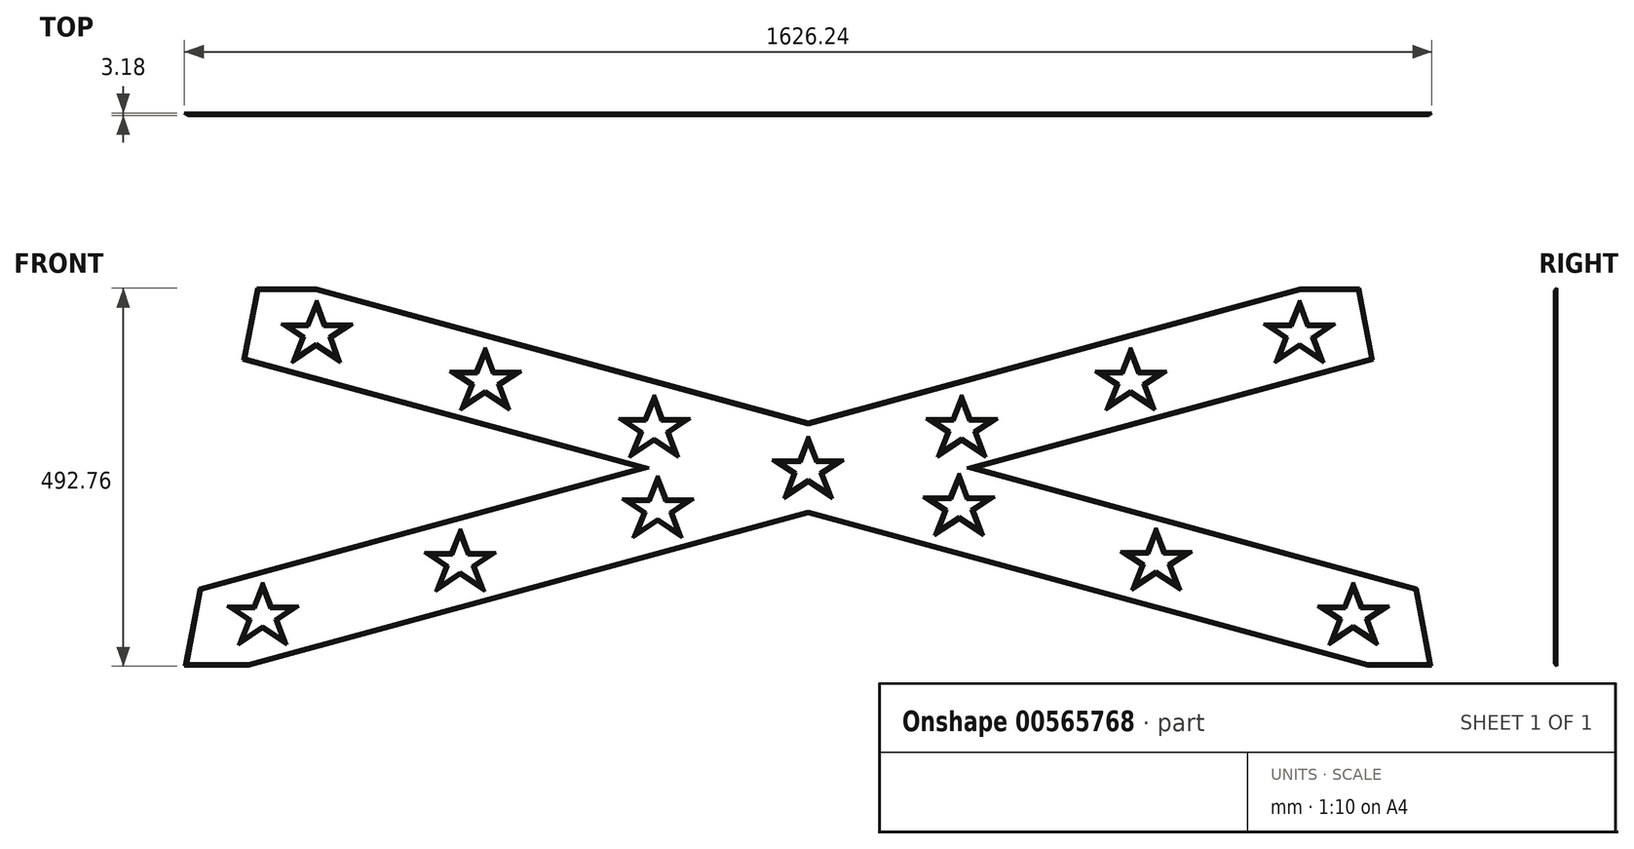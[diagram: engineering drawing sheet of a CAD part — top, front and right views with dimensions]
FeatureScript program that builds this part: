
annotation { "Feature Type Name" : "Feature", "Feature Type Description" : "" }
export const myFeature = defineFeature(function(context is Context, id is Id, definition is map)
    precondition{}
    {
        {
            var Q0;
            Q0=qCreatedBy(makeId("Front.planeOp"),FACE);
            var sketch = newSketch(context, id + "F0", { "sketchPlane" : qUnion([Q0])});
            skLineSegment(sketch, "E0", {"start": v(-830, -263.65) * mm, "end": v(830, -263.65) * mm});
            skLineSegment(sketch, "E1", {"start": v(830, -263.65) * mm, "end": v(730.63, 257.05) * mm});
            skLineSegment(sketch, "E2", {"start": v(730.63, 257.05) * mm, "end": v(-730.63, 257.05) * mm});
            skLineSegment(sketch, "E3", {"start": v(-730.63, 257.05) * mm, "end": v(-830, -263.65) * mm});
            skLineSegment(sketch, "E4", {"start": v(-738.12, 143.28) * mm, "end": v(-792.33, -140.76) * mm});
            skLineSegment(sketch, "E5", {"start": v(-705.17, -249.68) * mm, "end": v(705.17, -249.68) * mm});
            skLineSegment(sketch, "E6", {"start": v(-617.48, 243.08) * mm, "end": v(617.48, 243.08) * mm});
            skLineSegment(sketch, "E7", {"start": v(792.33, -140.76) * mm, "end": v(738.12, 143.28) * mm});
            skLineSegment(sketch, "E8", {"start": v(-738.12, 143.28) * mm, "end": v(-243.6, 8.64) * mm});
            skLineSegment(sketch, "E9", {"start": v(792.33, -140.76) * mm, "end": v(243.6, 8.64) * mm});
            skLineSegment(sketch, "E10", {"start": v(-792.33, -140.76) * mm, "end": v(-243.6, 8.64) * mm});
            skLineSegment(sketch, "E11", {"start": v(738.12, 143.28) * mm, "end": v(243.6, 8.64) * mm});
            skLineSegment(sketch, "E12.trimOffspring", {"start": v(0, 74.96) * mm, "end": v(617.48, 243.08) * mm});
            skLineSegment(sketch, "E13.trimOffspring", {"start": v(0, -57.68) * mm, "end": v(705.17, -249.68) * mm});
            skLineSegment(sketch, "E14.trimOffspring", {"start": v(0, 74.96) * mm, "end": v(-617.48, 243.08) * mm});
            skLineSegment(sketch, "E15.trimOffspring", {"start": v(0, -57.68) * mm, "end": v(-705.17, -249.68) * mm});
            skPoint(sketch, "E16.orphan", {"position": v(813.12, -249.68) * mm});
            skPoint(sketch, "E17.orphan", {"position": v(719.08, 243.08) * mm});
            skPoint(sketch, "E18.orphan", {"position": v(-719.08, 243.08) * mm});
            skPoint(sketch, "E19.orphan", {"position": v(-813.12, -249.68) * mm});
            skSolve(sketch);
        }
        {
            var Q0;
            Q0=makeQuery(id+"F0.imprint","IMPRINT",FACE,{"disambiguationData":[TD([[makeQuery(id+"F0.imprint","IMPRINT",EDGE,{"derivedFrom":sQuery(id+"F0.wireOp",EDGE,"E0")}),1.0]])]});
            var sketch = newSketch(context, id + "F1", { "sketchPlane" : qUnion([Q0])});
            skLineSegment(sketch, "E20", {"start": v(-736.93, 149.54) * mm, "end": v(-719.08, 243.08) * mm});
            skLineSegment(sketch, "E21", {"start": v(-719.08, 243.08) * mm, "end": v(-641.65, 243.08) * mm});
            skLineSegment(sketch, "E22", {"start": v(-641.65, 243.08) * mm, "end": v(0, 68.38) * mm});
            skLineSegment(sketch, "E23", {"start": v(0, 68.38) * mm, "end": v(641.65, 243.08) * mm});
            skLineSegment(sketch, "E24", {"start": v(641.65, 243.08) * mm, "end": v(719.08, 243.08) * mm});
            skLineSegment(sketch, "E25", {"start": v(719.08, 243.08) * mm, "end": v(736.93, 149.54) * mm});
            skLineSegment(sketch, "E26", {"start": v(736.93, 149.54) * mm, "end": v(219.43, 8.64) * mm});
            skLineSegment(sketch, "E27", {"start": v(219.43, 8.64) * mm, "end": v(793.66, -147.7) * mm});
            skLineSegment(sketch, "E28", {"start": v(793.66, -147.7) * mm, "end": v(813.12, -249.68) * mm});
            skLineSegment(sketch, "E29", {"start": v(813.12, -249.68) * mm, "end": v(729.34, -249.68) * mm});
            skLineSegment(sketch, "E30", {"start": v(729.34, -249.68) * mm, "end": v(0, -51.1) * mm});
            skLineSegment(sketch, "E31", {"start": v(0, -51.1) * mm, "end": v(-729.34, -249.68) * mm});
            skLineSegment(sketch, "E32", {"start": v(-729.34, -249.68) * mm, "end": v(-813.12, -249.68) * mm});
            skLineSegment(sketch, "E33", {"start": v(-813.12, -249.68) * mm, "end": v(-793.66, -147.7) * mm});
            skLineSegment(sketch, "E34", {"start": v(-793.66, -147.7) * mm, "end": v(-219.43, 8.64) * mm});
            skLineSegment(sketch, "E35", {"start": v(-219.43, 8.64) * mm, "end": v(-736.93, 149.54) * mm});
            skSolve(sketch);
        }
        {
            var Q0;
            Q0 = qSketchRegion(id + "F1", true);
            extrude(context, id + "F2", {"entities" : qUnion([Q0]), "depth" : 3.17 * mm, "offsetDistance" : 25.4 * mm});
        }
        {
            var Q0;
            Q0=makeQuery(id+"F2.opExtrude","CAP_FACE",FACE,{"disambiguationData":[OSD([sQuery(id+"F1.wireOp",EDGE,"E20"),sQuery(id+"F1.wireOp",EDGE,"E21"),sQuery(id+"F1.wireOp",EDGE,"E22"),sQuery(id+"F1.wireOp",EDGE,"E23"),sQuery(id+"F1.wireOp",EDGE,"E24"),sQuery(id+"F1.wireOp",EDGE,"E25"),sQuery(id+"F1.wireOp",EDGE,"E26"),sQuery(id+"F1.wireOp",EDGE,"E27"),sQuery(id+"F1.wireOp",EDGE,"E28"),sQuery(id+"F1.wireOp",EDGE,"E29"),sQuery(id+"F1.wireOp",EDGE,"E30"),sQuery(id+"F1.wireOp",EDGE,"E31"),sQuery(id+"F1.wireOp",EDGE,"E32"),sQuery(id+"F1.wireOp",EDGE,"E33"),sQuery(id+"F1.wireOp",EDGE,"E34"),sQuery(id+"F1.wireOp",EDGE,"E35")])],"isStart":false});
            var sketch = newSketch(context, id + "F3", { "sketchPlane" : qUnion([Q0])});
            skLineSegment(sketch, "E36.3.0.0", {"start": v(-651.4, 193.24) * mm, "end": v(-641.14, 218.64) * mm});
            skLineSegment(sketch, "E36.3.0.1", {"start": v(-631.77, 193.24) * mm, "end": v(-604.51, 193.24) * mm});
            skLineSegment(sketch, "E36.3.0.2", {"start": v(-641.14, 218.64) * mm, "end": v(-631.77, 193.24) * mm});
            skLineSegment(sketch, "E36.3.0.3", {"start": v(-604.51, 193.24) * mm, "end": v(-625.1, 179.5) * mm});
            skLineSegment(sketch, "E36.3.0.4", {"start": v(-625.1, 179.5) * mm, "end": v(-615.74, 154.1) * mm});
            skLineSegment(sketch, "E36.3.0.5", {"start": v(-615.74, 154.1) * mm, "end": v(-641.14, 171.05) * mm});
            skLineSegment(sketch, "E36.3.0.6", {"start": v(-641.14, 171.05) * mm, "end": v(-666.54, 154.1) * mm});
            skLineSegment(sketch, "E36.3.0.7", {"start": v(-666.54, 154.1) * mm, "end": v(-656.28, 179.5) * mm});
            skLineSegment(sketch, "E36.3.0.8", {"start": v(-656.28, 179.5) * mm, "end": v(-676.87, 193.24) * mm});
            skLineSegment(sketch, "E36.3.0.9", {"start": v(-676.87, 193.24) * mm, "end": v(-651.4, 193.24) * mm});
            skLineSegment(sketch, "E37.1.0.0", {"start": v(-446.42, 92.4) * mm, "end": v(-436.16, 117.8) * mm});
            skLineSegment(sketch, "E37.1.0.1", {"start": v(-421.02, 109.36) * mm, "end": v(-446.42, 92.4) * mm});
            skLineSegment(sketch, "E37.1.0.2", {"start": v(-395.62, 92.4) * mm, "end": v(-421.02, 109.36) * mm});
            skLineSegment(sketch, "E37.1.0.3", {"start": v(-404.99, 117.8) * mm, "end": v(-395.62, 92.4) * mm});
            skLineSegment(sketch, "E37.1.0.4", {"start": v(-384.4, 131.55) * mm, "end": v(-404.99, 117.8) * mm});
            skLineSegment(sketch, "E37.1.0.5", {"start": v(-411.65, 131.55) * mm, "end": v(-384.4, 131.55) * mm});
            skLineSegment(sketch, "E37.1.0.6", {"start": v(-421.02, 156.95) * mm, "end": v(-411.65, 131.55) * mm});
            skLineSegment(sketch, "E37.1.0.7", {"start": v(-431.28, 131.55) * mm, "end": v(-421.02, 156.95) * mm});
            skLineSegment(sketch, "E37.1.0.8", {"start": v(-456.75, 131.55) * mm, "end": v(-431.28, 131.55) * mm});
            skLineSegment(sketch, "E37.1.0.9", {"start": v(-436.16, 117.8) * mm, "end": v(-456.75, 131.55) * mm});
            skLineSegment(sketch, "E37.2.0.0", {"start": v(-226.3, 30.71) * mm, "end": v(-216.04, 56.11) * mm});
            skLineSegment(sketch, "E37.2.0.1", {"start": v(-200.9, 47.67) * mm, "end": v(-226.3, 30.71) * mm});
            skLineSegment(sketch, "E37.2.0.2", {"start": v(-175.5, 30.71) * mm, "end": v(-200.9, 47.67) * mm});
            skLineSegment(sketch, "E37.2.0.3", {"start": v(-184.87, 56.11) * mm, "end": v(-175.5, 30.71) * mm});
            skLineSegment(sketch, "E37.2.0.4", {"start": v(-164.27, 69.86) * mm, "end": v(-184.87, 56.11) * mm});
            skLineSegment(sketch, "E37.2.0.5", {"start": v(-191.53, 69.86) * mm, "end": v(-164.27, 69.86) * mm});
            skLineSegment(sketch, "E37.2.0.6", {"start": v(-200.9, 95.26) * mm, "end": v(-191.53, 69.86) * mm});
            skLineSegment(sketch, "E37.2.0.7", {"start": v(-211.16, 69.86) * mm, "end": v(-200.9, 95.26) * mm});
            skLineSegment(sketch, "E37.2.0.8", {"start": v(-236.63, 69.86) * mm, "end": v(-211.16, 69.86) * mm});
            skLineSegment(sketch, "E37.2.0.9", {"start": v(-216.04, 56.11) * mm, "end": v(-236.63, 69.86) * mm});
            skLineSegment(sketch, "E37.direction1", {"start": v(-666.54, 154.1) * mm, "end": v(-446.42, 92.4) * mm, "construction": true});
            skLineSegment(sketch, "E38.3.0.0", {"start": v(-721.15, -174.63) * mm, "end": v(-711.11, -149.23) * mm});
            skLineSegment(sketch, "E38.3.0.1", {"start": v(-701.51, -174.63) * mm, "end": v(-674.72, -174.63) * mm});
            skLineSegment(sketch, "E38.3.0.2", {"start": v(-711.11, -149.23) * mm, "end": v(-701.51, -174.63) * mm});
            skLineSegment(sketch, "E38.3.0.3", {"start": v(-674.72, -174.63) * mm, "end": v(-695.31, -188.38) * mm});
            skLineSegment(sketch, "E38.3.0.4", {"start": v(-695.31, -188.38) * mm, "end": v(-685.71, -213.78) * mm});
            skLineSegment(sketch, "E38.3.0.5", {"start": v(-685.71, -213.78) * mm, "end": v(-711.11, -196.82) * mm});
            skLineSegment(sketch, "E38.3.0.6", {"start": v(-711.11, -196.82) * mm, "end": v(-736.51, -213.78) * mm});
            skLineSegment(sketch, "E38.3.0.7", {"start": v(-736.51, -213.78) * mm, "end": v(-726.48, -188.38) * mm});
            skLineSegment(sketch, "E38.3.0.8", {"start": v(-726.48, -188.38) * mm, "end": v(-747.08, -174.63) * mm});
            skLineSegment(sketch, "E38.3.0.9", {"start": v(-747.08, -174.63) * mm, "end": v(-721.15, -174.63) * mm});
            skLineSegment(sketch, "E39.1.0.0", {"start": v(-437.88, -118.68) * mm, "end": v(-428.28, -144.08) * mm});
            skLineSegment(sketch, "E39.1.0.1", {"start": v(-417.29, -104.93) * mm, "end": v(-437.88, -118.68) * mm});
            skLineSegment(sketch, "E39.1.0.2", {"start": v(-444.08, -104.93) * mm, "end": v(-417.29, -104.93) * mm});
            skLineSegment(sketch, "E39.1.0.3", {"start": v(-453.68, -79.53) * mm, "end": v(-444.08, -104.93) * mm});
            skLineSegment(sketch, "E39.1.0.4", {"start": v(-463.72, -104.93) * mm, "end": v(-453.68, -79.53) * mm});
            skLineSegment(sketch, "E39.1.0.5", {"start": v(-489.65, -104.93) * mm, "end": v(-463.72, -104.93) * mm});
            skLineSegment(sketch, "E39.1.0.6", {"start": v(-469.05, -118.68) * mm, "end": v(-489.65, -104.93) * mm});
            skLineSegment(sketch, "E39.1.0.7", {"start": v(-479.08, -144.08) * mm, "end": v(-469.05, -118.68) * mm});
            skLineSegment(sketch, "E39.1.0.8", {"start": v(-453.68, -127.12) * mm, "end": v(-479.08, -144.08) * mm});
            skLineSegment(sketch, "E39.1.0.9", {"start": v(-428.28, -144.08) * mm, "end": v(-453.68, -127.12) * mm});
            skLineSegment(sketch, "E39.2.0.0", {"start": v(-180.45, -48.97) * mm, "end": v(-170.85, -74.37) * mm});
            skLineSegment(sketch, "E39.2.0.1", {"start": v(-159.86, -35.22) * mm, "end": v(-180.45, -48.97) * mm});
            skLineSegment(sketch, "E39.2.0.2", {"start": v(-186.65, -35.22) * mm, "end": v(-159.86, -35.22) * mm});
            skLineSegment(sketch, "E39.2.0.3", {"start": v(-196.25, -9.82) * mm, "end": v(-186.65, -35.22) * mm});
            skLineSegment(sketch, "E39.2.0.4", {"start": v(-206.28, -35.22) * mm, "end": v(-196.25, -9.82) * mm});
            skLineSegment(sketch, "E39.2.0.5", {"start": v(-232.22, -35.22) * mm, "end": v(-206.28, -35.22) * mm});
            skLineSegment(sketch, "E39.2.0.6", {"start": v(-211.62, -48.97) * mm, "end": v(-232.22, -35.22) * mm});
            skLineSegment(sketch, "E39.2.0.7", {"start": v(-221.65, -74.37) * mm, "end": v(-211.62, -48.97) * mm});
            skLineSegment(sketch, "E39.2.0.8", {"start": v(-196.25, -57.42) * mm, "end": v(-221.65, -74.37) * mm});
            skLineSegment(sketch, "E39.2.0.9", {"start": v(-170.85, -74.37) * mm, "end": v(-196.25, -57.42) * mm});
            skLineSegment(sketch, "E39.direction1", {"start": v(-685.71, -213.78) * mm, "end": v(-428.28, -144.08) * mm, "construction": true});
            skLineSegment(sketch, "E40.3.0.0", {"start": v(630.48, 193.07) * mm, "end": v(640.5, 218.47) * mm});
            skLineSegment(sketch, "E40.3.0.1", {"start": v(650.1, 193.07) * mm, "end": v(676.9, 193.07) * mm});
            skLineSegment(sketch, "E40.3.0.2", {"start": v(640.5, 218.47) * mm, "end": v(650.1, 193.07) * mm});
            skLineSegment(sketch, "E40.3.0.3", {"start": v(676.9, 193.07) * mm, "end": v(656.3, 179.32) * mm});
            skLineSegment(sketch, "E40.3.0.4", {"start": v(656.3, 179.32) * mm, "end": v(665.9, 153.92) * mm});
            skLineSegment(sketch, "E40.3.0.5", {"start": v(665.9, 153.92) * mm, "end": v(640.5, 170.88) * mm});
            skLineSegment(sketch, "E40.3.0.6", {"start": v(640.5, 170.88) * mm, "end": v(615.1, 153.92) * mm});
            skLineSegment(sketch, "E40.3.0.7", {"start": v(615.1, 153.92) * mm, "end": v(625.14, 179.32) * mm});
            skLineSegment(sketch, "E40.3.0.8", {"start": v(625.14, 179.32) * mm, "end": v(604.54, 193.07) * mm});
            skLineSegment(sketch, "E40.3.0.9", {"start": v(604.54, 193.07) * mm, "end": v(630.48, 193.07) * mm});
            skLineSegment(sketch, "E41.1.0.0", {"start": v(420.34, 156.96) * mm, "end": v(429.94, 131.56) * mm});
            skLineSegment(sketch, "E41.1.0.1", {"start": v(429.94, 131.56) * mm, "end": v(456.74, 131.56) * mm});
            skLineSegment(sketch, "E41.1.0.2", {"start": v(456.74, 131.56) * mm, "end": v(436.14, 117.8) * mm});
            skLineSegment(sketch, "E41.1.0.3", {"start": v(436.14, 117.8) * mm, "end": v(445.74, 92.4) * mm});
            skLineSegment(sketch, "E41.1.0.4", {"start": v(445.74, 92.4) * mm, "end": v(420.34, 109.37) * mm});
            skLineSegment(sketch, "E41.1.0.5", {"start": v(420.34, 109.37) * mm, "end": v(394.94, 92.4) * mm});
            skLineSegment(sketch, "E41.1.0.6", {"start": v(394.94, 92.4) * mm, "end": v(404.97, 117.8) * mm});
            skLineSegment(sketch, "E41.1.0.7", {"start": v(404.97, 117.8) * mm, "end": v(384.37, 131.56) * mm});
            skLineSegment(sketch, "E41.1.0.8", {"start": v(384.37, 131.56) * mm, "end": v(410.3, 131.56) * mm});
            skLineSegment(sketch, "E41.1.0.9", {"start": v(410.3, 131.56) * mm, "end": v(420.34, 156.96) * mm});
            skLineSegment(sketch, "E41.2.0.0", {"start": v(200.17, 95.45) * mm, "end": v(209.77, 70.05) * mm});
            skLineSegment(sketch, "E41.2.0.1", {"start": v(209.77, 70.05) * mm, "end": v(236.57, 70.05) * mm});
            skLineSegment(sketch, "E41.2.0.2", {"start": v(236.57, 70.05) * mm, "end": v(215.97, 56.3) * mm});
            skLineSegment(sketch, "E41.2.0.3", {"start": v(215.97, 56.3) * mm, "end": v(225.57, 30.9) * mm});
            skLineSegment(sketch, "E41.2.0.4", {"start": v(225.57, 30.9) * mm, "end": v(200.17, 47.85) * mm});
            skLineSegment(sketch, "E41.2.0.5", {"start": v(200.17, 47.85) * mm, "end": v(174.77, 30.9) * mm});
            skLineSegment(sketch, "E41.2.0.6", {"start": v(174.77, 30.9) * mm, "end": v(184.8, 56.3) * mm});
            skLineSegment(sketch, "E41.2.0.7", {"start": v(184.8, 56.3) * mm, "end": v(164.2, 70.05) * mm});
            skLineSegment(sketch, "E41.2.0.8", {"start": v(164.2, 70.05) * mm, "end": v(190.14, 70.05) * mm});
            skLineSegment(sketch, "E41.2.0.9", {"start": v(190.14, 70.05) * mm, "end": v(200.17, 95.45) * mm});
            skLineSegment(sketch, "E41.direction1", {"start": v(650.1, 193.07) * mm, "end": v(429.94, 131.56) * mm, "construction": true});
            skLineSegment(sketch, "E42.3.0.0", {"start": v(700.63, -174.5) * mm, "end": v(710.66, -149.1) * mm});
            skLineSegment(sketch, "E42.3.0.1", {"start": v(720.26, -174.5) * mm, "end": v(747.06, -174.5) * mm});
            skLineSegment(sketch, "E42.3.0.2", {"start": v(710.66, -149.1) * mm, "end": v(720.26, -174.5) * mm});
            skLineSegment(sketch, "E42.3.0.3", {"start": v(747.06, -174.5) * mm, "end": v(726.46, -188.26) * mm});
            skLineSegment(sketch, "E42.3.0.4", {"start": v(726.46, -188.26) * mm, "end": v(736.06, -213.66) * mm});
            skLineSegment(sketch, "E42.3.0.5", {"start": v(736.06, -213.66) * mm, "end": v(710.66, -196.7) * mm});
            skLineSegment(sketch, "E42.3.0.6", {"start": v(710.66, -196.7) * mm, "end": v(685.26, -213.66) * mm});
            skLineSegment(sketch, "E42.3.0.7", {"start": v(685.26, -213.66) * mm, "end": v(695.3, -188.26) * mm});
            skLineSegment(sketch, "E42.3.0.8", {"start": v(695.3, -188.26) * mm, "end": v(674.7, -174.5) * mm});
            skLineSegment(sketch, "E42.3.0.9", {"start": v(674.7, -174.5) * mm, "end": v(700.63, -174.5) * mm});
            skLineSegment(sketch, "E43.1.0.0", {"start": v(479.03, -142.47) * mm, "end": v(453.63, -125.52) * mm});
            skLineSegment(sketch, "E43.1.0.1", {"start": v(469.43, -117.07) * mm, "end": v(479.03, -142.47) * mm});
            skLineSegment(sketch, "E43.1.0.2", {"start": v(490.03, -103.32) * mm, "end": v(469.43, -117.07) * mm});
            skLineSegment(sketch, "E43.1.0.3", {"start": v(463.23, -103.32) * mm, "end": v(490.03, -103.32) * mm});
            skLineSegment(sketch, "E43.1.0.4", {"start": v(453.63, -77.92) * mm, "end": v(463.23, -103.32) * mm});
            skLineSegment(sketch, "E43.1.0.5", {"start": v(443.6, -103.32) * mm, "end": v(453.63, -77.92) * mm});
            skLineSegment(sketch, "E43.1.0.6", {"start": v(417.67, -103.32) * mm, "end": v(443.6, -103.32) * mm});
            skLineSegment(sketch, "E43.1.0.7", {"start": v(438.27, -117.07) * mm, "end": v(417.67, -103.32) * mm});
            skLineSegment(sketch, "E43.1.0.8", {"start": v(428.23, -142.47) * mm, "end": v(438.27, -117.07) * mm});
            skLineSegment(sketch, "E43.1.0.9", {"start": v(453.63, -125.52) * mm, "end": v(428.23, -142.47) * mm});
            skLineSegment(sketch, "E43.2.0.0", {"start": v(222, -71.3) * mm, "end": v(196.6, -54.33) * mm});
            skLineSegment(sketch, "E43.2.0.1", {"start": v(212.4, -45.9) * mm, "end": v(222, -71.3) * mm});
            skLineSegment(sketch, "E43.2.0.2", {"start": v(233, -32.14) * mm, "end": v(212.4, -45.9) * mm});
            skLineSegment(sketch, "E43.2.0.3", {"start": v(206.2, -32.14) * mm, "end": v(233, -32.14) * mm});
            skLineSegment(sketch, "E43.2.0.4", {"start": v(196.6, -6.74) * mm, "end": v(206.2, -32.14) * mm});
            skLineSegment(sketch, "E43.2.0.5", {"start": v(186.58, -32.14) * mm, "end": v(196.6, -6.74) * mm});
            skLineSegment(sketch, "E43.2.0.6", {"start": v(160.64, -32.14) * mm, "end": v(186.58, -32.14) * mm});
            skLineSegment(sketch, "E43.2.0.7", {"start": v(181.24, -45.9) * mm, "end": v(160.64, -32.14) * mm});
            skLineSegment(sketch, "E43.2.0.8", {"start": v(171.2, -71.3) * mm, "end": v(181.24, -45.9) * mm});
            skLineSegment(sketch, "E43.2.0.9", {"start": v(196.6, -54.33) * mm, "end": v(171.2, -71.3) * mm});
            skLineSegment(sketch, "E43.direction1", {"start": v(710.66, -196.7) * mm, "end": v(453.63, -125.52) * mm, "construction": true});
            skLineSegment(sketch, "E44.3.0.0", {"start": v(-9.68, 16.04) * mm, "end": v(0, 41.44) * mm});
            skLineSegment(sketch, "E44.3.0.1", {"start": v(9.96, 16.04) * mm, "end": v(36.04, 16.04) * mm});
            skLineSegment(sketch, "E44.3.0.2", {"start": v(0, 41.44) * mm, "end": v(9.96, 16.04) * mm});
            skLineSegment(sketch, "E44.3.0.3", {"start": v(36.04, 16.04) * mm, "end": v(15.44, 2.29) * mm});
            skLineSegment(sketch, "E44.3.0.4", {"start": v(15.44, 2.29) * mm, "end": v(25.4, -23.11) * mm});
            skLineSegment(sketch, "E44.3.0.5", {"start": v(25.4, -23.11) * mm, "end": v(0, -6.15) * mm});
            skLineSegment(sketch, "E44.3.0.6", {"start": v(0, -6.15) * mm, "end": v(-25.4, -23.11) * mm});
            skLineSegment(sketch, "E44.3.0.7", {"start": v(-25.4, -23.11) * mm, "end": v(-15.72, 2.29) * mm});
            skLineSegment(sketch, "E44.3.0.8", {"start": v(-15.72, 2.29) * mm, "end": v(-36.32, 16.04) * mm});
            skLineSegment(sketch, "E44.3.0.9", {"start": v(-36.32, 16.04) * mm, "end": v(-9.68, 16.04) * mm});
            skSolve(sketch);
        }
        {
            var Q0;
            Q0 = qSketchRegion(id + "F3", true);
            extrude(context, id + "F4", {"entities" : qUnion([Q0]), "operationType" : NewBodyOperationType.REMOVE, "oppositeDirection" : true, "depth" : 3.17 * mm, "offsetDistance" : 25.4 * mm});
        }
        {
            var Q0;
            Q0=makeQuery(id+"F2.opExtrude","CAP_FACE",FACE,{"disambiguationData":[OSD([sQuery(id+"F1.wireOp",EDGE,"E20"),sQuery(id+"F1.wireOp",EDGE,"E21"),sQuery(id+"F1.wireOp",EDGE,"E22"),sQuery(id+"F1.wireOp",EDGE,"E23"),sQuery(id+"F1.wireOp",EDGE,"E24"),sQuery(id+"F1.wireOp",EDGE,"E25"),sQuery(id+"F1.wireOp",EDGE,"E26"),sQuery(id+"F1.wireOp",EDGE,"E27"),sQuery(id+"F1.wireOp",EDGE,"E28"),sQuery(id+"F1.wireOp",EDGE,"E29"),sQuery(id+"F1.wireOp",EDGE,"E30"),sQuery(id+"F1.wireOp",EDGE,"E31"),sQuery(id+"F1.wireOp",EDGE,"E32"),sQuery(id+"F1.wireOp",EDGE,"E33"),sQuery(id+"F1.wireOp",EDGE,"E34"),sQuery(id+"F1.wireOp",EDGE,"E35")])],"isStart":false});
            chamfer(context, id + "F5", {"entities" : qUnion([Q0]), "width" : 3.17 * mm, "tangentPropagation" : true});
        }
    });
